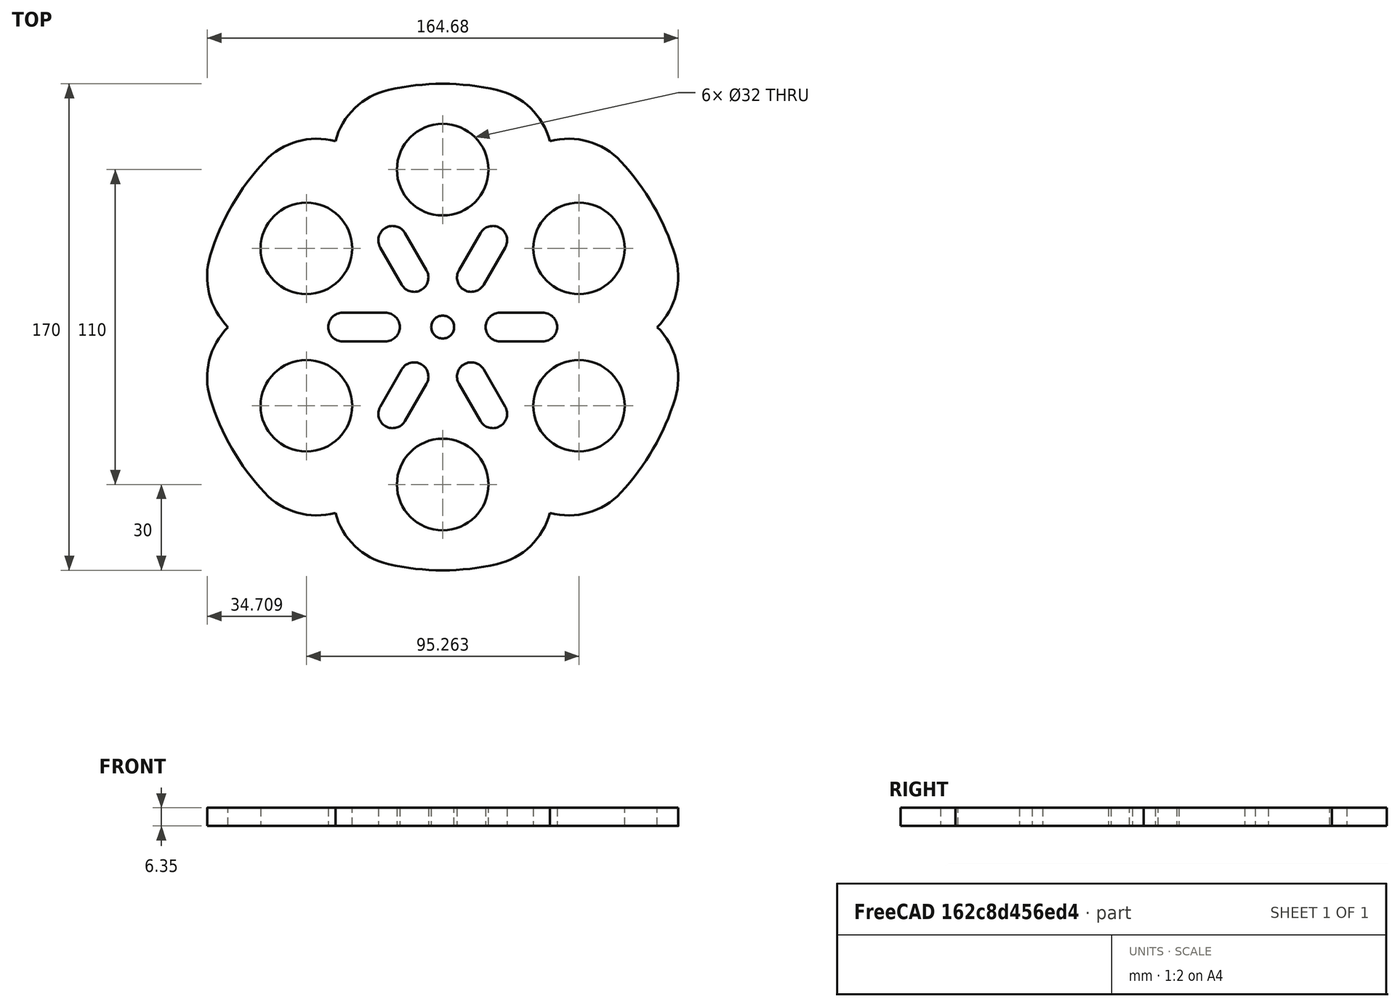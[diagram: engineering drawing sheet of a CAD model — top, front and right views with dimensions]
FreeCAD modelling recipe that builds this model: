
FCSTD DOCUMENT  (FreeCAD 0.21R33771 (Git))
Label: Tripod Pad
License: All rights reserved
LicenseURL: http://en.wikipedia.org/wiki/All_rights_reserved
objects: Sketcher::SketchObject×1, PartDesign::Pad×1, PartDesign::Body×1
note: 4 computed .brp shape members not serialized (recipe doc carries the construction recipe); baked Part::Feature solids carry a one-line shape summary decoded from their .brp

FEATURE [Sketcher::SketchObject] Sketch
  FullyConstrained = true
  MapMode = 5
  Support = -> [XY_Plane]
  sketch-geometry (58):
    g0: Circle CenterX=0 CenterY=0 CenterZ=0 NormalX=0 NormalY=0 NormalZ=1 AngleXU=0 Radius=75
    g1: LineSegment StartX=0 StartY=0 StartZ=0 EndX=-47.6314 EndY=-27.5 EndZ=0
    g2: LineSegment StartX=0 StartY=0 StartZ=0 EndX=47.6314 EndY=-27.5 EndZ=0
    g3: Circle CenterX=0 CenterY=0 CenterZ=0 NormalX=0 NormalY=0 NormalZ=1 AngleXU=0 Radius=4
    g4: Circle CenterX=-47.6314 CenterY=-27.5 CenterZ=0 NormalX=0 NormalY=0 NormalZ=1 AngleXU=0 Radius=16
    g5: Circle CenterX=47.6314 CenterY=-27.5 CenterZ=0 NormalX=0 NormalY=0 NormalZ=1 AngleXU=0 Radius=16
    g6: Circle CenterX=0 CenterY=55 CenterZ=0 NormalX=0 NormalY=0 NormalZ=1 AngleXU=0 Radius=16
    g7: Circle CenterX=0 CenterY=0 CenterZ=0 NormalX=0 NormalY=0 NormalZ=1 AngleXU=0 Radius=55
    g8: ArcOfCircle CenterX=-57.4152 CenterY=17.6683 CenterZ=0 NormalX=0 NormalY=0 NormalZ=1 AngleXU=0 Radius=24.9278 StartAngle=2.84306 EndAngle=3.92936
    g9: ArcOfCircle CenterX=-57.4152 CenterY=-17.6683 CenterZ=0 NormalX=0 NormalY=0 NormalZ=1 AngleXU=0 Radius=24.9278 StartAngle=2.35383 EndAngle=3.44012
    g10: ArcOfCircle CenterX=13.4064 CenterY=58.5571 CenterZ=0 NormalX=0 NormalY=0 NormalZ=1 AngleXU=0 Radius=24.9278 StartAngle=0.259432 EndAngle=1.34573
    g11: ArcOfCircle CenterX=44.0088 CenterY=40.8888 CenterZ=0 NormalX=0 NormalY=0 NormalZ=1 AngleXU=0 Radius=24.9278 StartAngle=0.748665 EndAngle=1.83496
    g12: ArcOfCircle CenterX=0 CenterY=0 CenterZ=0 NormalX=0 NormalY=0 NormalZ=1 AngleXU=0 Radius=85 StartAngle=1.34573 EndAngle=1.79586
    g13: ArcOfCircle CenterX=0 CenterY=0 CenterZ=0 NormalX=0 NormalY=0 NormalZ=1 AngleXU=0 Radius=85 StartAngle=5.53452 EndAngle=5.98465
    g14: ArcOfCircle CenterX=0 CenterY=0 CenterZ=0 NormalX=0 NormalY=0 NormalZ=1 AngleXU=0 Radius=85 StartAngle=3.44012 EndAngle=3.89026
    g15: Circle CenterX=-47.6314 CenterY=27.5 CenterZ=0 NormalX=0 NormalY=0 NormalZ=1 AngleXU=0 Radius=16
    g16: Circle CenterX=47.6314 CenterY=27.5 CenterZ=0 NormalX=0 NormalY=0 NormalZ=1 AngleXU=0 Radius=16
    g17: Circle CenterX=0 CenterY=-55 CenterZ=0 NormalX=0 NormalY=0 NormalZ=1 AngleXU=0 Radius=16
    g18: LineSegment StartX=0 StartY=0 StartZ=0 EndX=37.5 EndY=64.9519 EndZ=0
    g19: LineSegment StartX=0 StartY=0 StartZ=0 EndX=37.5 EndY=-64.9519 EndZ=0
    g20: ArcOfCircle CenterX=13.4064 CenterY=-58.5571 CenterZ=0 NormalX=0 NormalY=0 NormalZ=1 AngleXU=0 Radius=24.9278 StartAngle=4.93746 EndAngle=6.02375
    g21: ArcOfCircle CenterX=44.0088 CenterY=-40.8888 CenterZ=0 NormalX=0 NormalY=0 NormalZ=1 AngleXU=0 Radius=24.9278 StartAngle=4.44822 EndAngle=5.53452
    g22: Circle CenterX=0 CenterY=0 CenterZ=0 NormalX=0 NormalY=0 NormalZ=1 AngleXU=0 Radius=60.0722
    g23: ArcOfCircle CenterX=-13.4064 CenterY=-58.5571 CenterZ=0 NormalX=0 NormalY=0 NormalZ=1 AngleXU=0 Radius=24.9278 StartAngle=3.40102 EndAngle=4.48732
    g24: ArcOfCircle CenterX=-44.0088 CenterY=-40.8888 CenterZ=0 NormalX=0 NormalY=0 NormalZ=1 AngleXU=0 Radius=24.9278 StartAngle=3.89026 EndAngle=4.97656
    g25: ArcOfCircle CenterX=0 CenterY=0 CenterZ=0 NormalX=0 NormalY=0 NormalZ=1 AngleXU=0 Radius=85 StartAngle=4.48732 EndAngle=4.93746
    g26: ArcOfCircle CenterX=57.4152 CenterY=-17.6683 CenterZ=0 NormalX=0 NormalY=0 NormalZ=1 AngleXU=0 Radius=24.9278 StartAngle=5.98465 EndAngle=7.07095
    g27: ArcOfCircle CenterX=57.4152 CenterY=17.6683 CenterZ=0 NormalX=0 NormalY=0 NormalZ=1 AngleXU=0 Radius=24.9278 StartAngle=5.49542 EndAngle=6.58172
    g28: ArcOfCircle CenterX=0 CenterY=0 CenterZ=0 NormalX=0 NormalY=0 NormalZ=1 AngleXU=0 Radius=85 StartAngle=0.298532 EndAngle=0.748665
    g29: ArcOfCircle CenterX=-13.4064 CenterY=58.5571 CenterZ=0 NormalX=0 NormalY=0 NormalZ=1 AngleXU=0 Radius=24.9278 StartAngle=1.79586 EndAngle=2.88216
    g30: ArcOfCircle CenterX=-44.0088 CenterY=40.8888 CenterZ=0 NormalX=0 NormalY=0 NormalZ=1 AngleXU=0 Radius=24.9278 StartAngle=1.30663 EndAngle=2.39293
    g31: ArcOfCircle CenterX=0 CenterY=0 CenterZ=0 NormalX=0 NormalY=0 NormalZ=1 AngleXU=0 Radius=85 StartAngle=2.39293 EndAngle=2.84306
    g32: ArcOfCircle CenterX=-17.5 CenterY=30.3109 CenterZ=0 NormalX=0 NormalY=0 NormalZ=1 AngleXU=0 Radius=5 StartAngle=0.523599 EndAngle=3.66519
    g33: ArcOfCircle CenterX=-10 CenterY=17.3205 CenterZ=0 NormalX=0 NormalY=0 NormalZ=1 AngleXU=0 Radius=5 StartAngle=3.66519 EndAngle=6.80678
    g34: LineSegment StartX=-21.8301 StartY=27.8109 StartZ=0 EndX=-14.3301 EndY=14.8205 EndZ=0
    g35: LineSegment StartX=-5.66987 StartY=19.8205 StartZ=0 EndX=-13.1699 EndY=32.8109 EndZ=0
    g36: ArcOfCircle CenterX=17.5 CenterY=30.3109 CenterZ=0 NormalX=0 NormalY=0 NormalZ=1 AngleXU=0 Radius=5 StartAngle=5.75959 EndAngle=8.90118
    g37: ArcOfCircle CenterX=10 CenterY=17.3205 CenterZ=0 NormalX=0 NormalY=0 NormalZ=1 AngleXU=0 Radius=5 StartAngle=2.61799 EndAngle=5.75959
    g38: LineSegment StartX=13.1699 StartY=32.8109 StartZ=0 EndX=5.66987 EndY=19.8205 EndZ=0
    g39: LineSegment StartX=14.3301 StartY=14.8205 StartZ=0 EndX=21.8301 EndY=27.8109 EndZ=0
    g40: ArcOfCircle CenterX=35 CenterY=0 CenterZ=0 NormalX=0 NormalY=0 NormalZ=1 AngleXU=0 Radius=5 StartAngle=4.71239 EndAngle=7.85398
    g41: ArcOfCircle CenterX=20 CenterY=0 CenterZ=0 NormalX=0 NormalY=0 NormalZ=1 AngleXU=0 Radius=5 StartAngle=1.5708 EndAngle=4.71239
    g42: LineSegment StartX=35 StartY=5 StartZ=0 EndX=20 EndY=5 EndZ=0
    g43: LineSegment StartX=20 StartY=-5 StartZ=0 EndX=35 EndY=-5 EndZ=0
    g44: ArcOfCircle CenterX=10 CenterY=-17.3205 CenterZ=0 NormalX=0 NormalY=0 NormalZ=1 AngleXU=0 Radius=5 StartAngle=0.523599 EndAngle=3.66519
    g45: ArcOfCircle CenterX=17.5 CenterY=-30.3109 CenterZ=0 NormalX=0 NormalY=0 NormalZ=1 AngleXU=0 Radius=5 StartAngle=3.66519 EndAngle=6.80678
    g46: LineSegment StartX=5.66987 StartY=-19.8205 StartZ=0 EndX=13.1699 EndY=-32.8109 EndZ=0
    g47: LineSegment StartX=21.8301 StartY=-27.8109 StartZ=0 EndX=14.3301 EndY=-14.8205 EndZ=0
    g48: ArcOfCircle CenterX=-10 CenterY=-17.3205 CenterZ=0 NormalX=0 NormalY=0 NormalZ=1 AngleXU=0 Radius=5 StartAngle=5.75959 EndAngle=8.90118
    g49: ArcOfCircle CenterX=-17.5 CenterY=-30.3109 CenterZ=0 NormalX=0 NormalY=0 NormalZ=1 AngleXU=0 Radius=5 StartAngle=2.61799 EndAngle=5.75959
    g50: LineSegment StartX=-14.3301 StartY=-14.8205 StartZ=0 EndX=-21.8301 EndY=-27.8109 EndZ=0
    g51: LineSegment StartX=-13.1699 StartY=-32.8109 StartZ=0 EndX=-5.66987 EndY=-19.8205 EndZ=0
    g52: ArcOfCircle CenterX=-35 CenterY=0 CenterZ=0 NormalX=0 NormalY=0 NormalZ=1 AngleXU=0 Radius=5 StartAngle=1.5708 EndAngle=4.71239
    g53: ArcOfCircle CenterX=-20 CenterY=0 CenterZ=0 NormalX=0 NormalY=0 NormalZ=1 AngleXU=0 Radius=5 StartAngle=4.71239 EndAngle=7.85398
    g54: LineSegment StartX=-35 StartY=-5 StartZ=0 EndX=-20 EndY=-5 EndZ=0
    g55: LineSegment StartX=-20 StartY=5 StartZ=0 EndX=-35 EndY=5 EndZ=0
    g56: Circle CenterX=0 CenterY=0 CenterZ=0 NormalX=0 NormalY=0 NormalZ=1 AngleXU=0 Radius=20
    g57: Circle CenterX=0 CenterY=0 CenterZ=0 NormalX=0 NormalY=0 NormalZ=1 AngleXU=0 Radius=35
  constraints (152):
    c: Diameter(g0) = 150
    c: Angle(g2,g-2) = 2.0944
    c: Angle(g-2,g1) = 2.0944
    c: PointOnObject(g6,g-2)
    c: Equal(g5,g4)
    c: Equal(g4,g6)
    c: Diameter(g6) = 32
    c: Coincident(g7,g3)
    c: PointOnObject(g5,g7)
    c: PointOnObject(g4,g7)
    c: PointOnObject(g6,g7)
    c: Diameter(g3) = 8
    c: Coincident(g9,g8)
    c: Coincident(g11,g10)
    c: Coincident(g12,g3)
    c: Coincident(g13,g3)
    c: Coincident(g14,g3)
    c: PointOnObject(g15,g7)
    c: PointOnObject(g16,g7)
    c: PointOnObject(g17,g7)
    c: Equal(g17,g16)
    c: Equal(g16,g15)
    c: Equal(g15,g6)
    c: PointOnObject(g15,g2)
    c: PointOnObject(g16,g1)
    c: PointOnObject(g17,g-2)
    c: Distance(g6,g16) = 55
    c: Coincident(g18,g3)
    c: Coincident(g19,g3)
    c: Angle(g19,g18) = 2.0944
    c: PointOnObject(g8,g-1)
    c: Coincident(g21,g20)
    c: PointOnObject(g20,g0)
    c: Diameter(g13) = 170
    c: Coincident(g1,g2)
    c: Coincident(g1,g3)
    c: Coincident(g1,g0)
    c: Coincident(g3,g-1)
    c: Coincident(g19,g20)
    c: Coincident(g1,g4)
    c: Coincident(g18,g10)
    c: Coincident(g2,g5)
    c: Equal(g12,g13)
    c: Equal(g13,g14)
    c: Coincident(g22,g3)
    c: PointOnObject(g20,g22)
    c: PointOnObject(g9,g22)
    c: PointOnObject(g8,g22)
    c: PointOnObject(g10,g22)
    c: PointOnObject(g11,g22)
    c: PointOnObject(g21,g22)
    c: PointOnObject(g8,g0)
    c: Angle(g19,g-1) = 1.0472
    c: Tangent(g14,g9) = -1.5708
    c: Tangent(g10,g12) = -1.5708
    c: Tangent(g21,g13) = -1.5708
    c: PointOnObject(g10,g0)
    c: Distance(g8,g9) = 50
    c: PointOnObject(g23,g22)
    c: PointOnObject(g23,g0)
    c: PointOnObject(g24,g22)
    c: Coincident(g23,g24)
    c: PointOnObject(g23,g18)
    c: Equal(g14,g25)
    c: Tangent(g14,g24) = -1.5708
    c: Tangent(g25,g23) = -1.5708
    c: Coincident(g14,g25)
    c: Tangent(g20,g25) = -1.5708
    c: PointOnObject(g26,g22)
    c: PointOnObject(g26,g0)
    c: PointOnObject(g27,g22)
    c: Coincident(g26,g27)
    c: PointOnObject(g26,g-1)
    c: Equal(g13,g28)
    c: Tangent(g13,g26) = -1.5708
    c: Tangent(g28,g27) = -1.5708
    c: Coincident(g13,g28)
    c: Tangent(g28,g11) = -1.5708
    c: PointOnObject(g29,g22)
    c: PointOnObject(g29,g0)
    c: PointOnObject(g30,g22)
    c: Coincident(g30,g29)
    c: Equal(g12,g31)
    c: Tangent(g12,g29) = -1.5708
    c: Tangent(g31,g30) = -1.5708
    c: Coincident(g12,g31)
    c: PointOnObject(g29,g19)
    c: Tangent(g8,g31) = -1.5708
    c: Tangent(g32,g34) = -1.5708
    c: Tangent(g34,g33) = -1.5708
    c: Tangent(g33,g35) = -1.5708
    c: Tangent(g35,g32) = -1.5708
    c: Equal(g32,g33)
    c: Tangent(g36,g38) = -1.5708
    c: Tangent(g38,g37) = -1.5708
    c: Tangent(g37,g39) = -1.5708
    c: Tangent(g39,g36) = -1.5708
    c: Equal(g36,g37)
    c: PointOnObject(g36,g18)
    c: PointOnObject(g37,g18)
    c: Tangent(g40,g42) = -1.5708
    c: Tangent(g42,g41) = -1.5708
    c: Tangent(g41,g43) = -1.5708
    c: Tangent(g43,g40) = -1.5708
    c: Equal(g40,g41)
    c: PointOnObject(g40,g-1)
    c: PointOnObject(g41,g-1)
    c: Tangent(g44,g46) = -1.5708
    c: Tangent(g46,g45) = -1.5708
    c: Tangent(g45,g47) = -1.5708
    c: Tangent(g47,g44) = -1.5708
    c: Equal(g44,g45)
    c: PointOnObject(g44,g19)
    c: PointOnObject(g45,g19)
    c: Tangent(g48,g50) = -1.5708
    c: Tangent(g50,g49) = -1.5708
    c: Tangent(g49,g51) = -1.5708
    c: Tangent(g51,g48) = -1.5708
    c: Equal(g48,g49)
    c: Tangent(g52,g54) = -1.5708
    c: Tangent(g54,g53) = -1.5708
    c: Tangent(g53,g55) = -1.5708
    c: Tangent(g55,g52) = -1.5708
    c: Equal(g52,g53)
    c: PointOnObject(g52,g-1)
    c: PointOnObject(g53,g-1)
    c: Coincident(g56,g3)
    c: PointOnObject(g37,g56)
    c: PointOnObject(g33,g56)
    c: PointOnObject(g53,g56)
    c: PointOnObject(g48,g56)
    c: PointOnObject(g44,g56)
    c: PointOnObject(g41,g56)
    c: PointOnObject(g48,g18)
    c: PointOnObject(g49,g18)
    c: Equal(g41,g44)
    c: Equal(g44,g48)
    c: Equal(g48,g53)
    c: Equal(g53,g33)
    c: Equal(g33,g37)
    c: PointOnObject(g32,g19)
    c: PointOnObject(g33,g19)
    c: Coincident(g57,g3)
    c: PointOnObject(g40,g57)
    c: PointOnObject(g45,g57)
    c: PointOnObject(g49,g57)
    c: PointOnObject(g52,g57)
    c: PointOnObject(g32,g57)
    c: PointOnObject(g36,g57)
    c: Diameter(g32) = 10
    c: Diameter(g56) = 40
    c: Diameter(g57) = 70
FEATURE [PartDesign::Pad] Pad
  Direction = (0,0,1)
  Length = 6.35
  Length2 = 10
  Profile = -> Sketch
  ReferenceAxis = -> Sketch [N_Axis]
  Type = 0
FEATURE [PartDesign::Body] Body
  Group = -> [Sketch,Pad]
  Origin = -> Origin
  Tip = -> Pad
